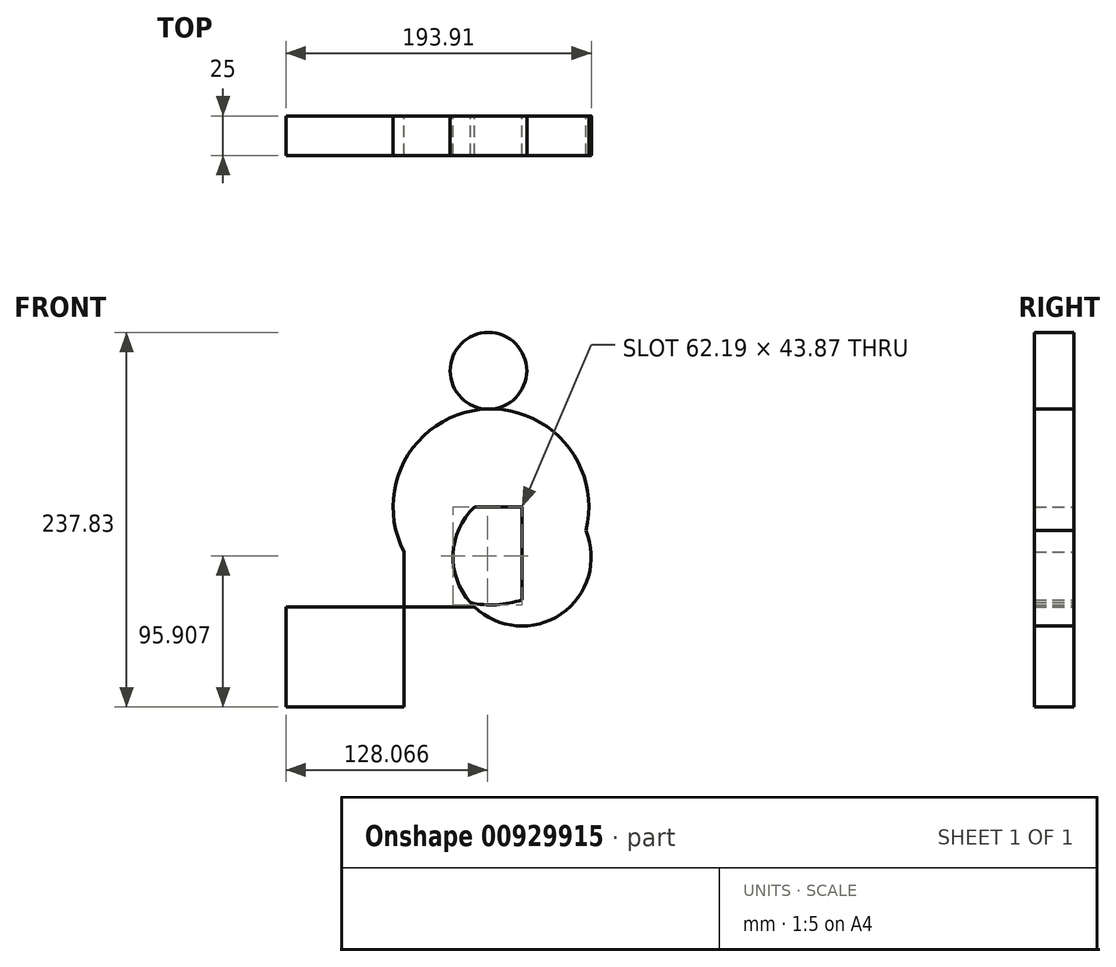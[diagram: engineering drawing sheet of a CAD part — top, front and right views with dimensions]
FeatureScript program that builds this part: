
annotation { "Feature Type Name" : "Feature", "Feature Type Description" : "" }
export const myFeature = defineFeature(function(context is Context, id is Id, definition is map)
    precondition{}
    {
        {
            var Q0;
            Q0=qCreatedBy(makeId("Front.planeOp"),FACE);
            var sketch = newSketch(context, id + "F0", { "sketchPlane" : qUnion([Q0])});
            skLineSegment(sketch, "E0.bottom", {"start": v(0, 0) * mm, "end": v(75, 0) * mm});
            skLineSegment(sketch, "E0.top", {"start": v(0, 63.5) * mm, "end": v(75, 63.5) * mm});
            skLineSegment(sketch, "E0.left", {"start": v(0, 0) * mm, "end": v(0, 63.5) * mm});
            skLineSegment(sketch, "E0.right", {"start": v(75, 0) * mm, "end": v(75, 63.5) * mm});
            skLineSegment(sketch, "E1.bottom", {"start": v(0, 0) * mm, "end": v(-75, 0) * mm});
            skLineSegment(sketch, "E1.top", {"start": v(0, -63.5) * mm, "end": v(-75, -63.5) * mm});
            skLineSegment(sketch, "E1.left", {"start": v(0, 0) * mm, "end": v(0, -63.5) * mm});
            skLineSegment(sketch, "E1.right", {"start": v(-75, 0) * mm, "end": v(-75, -63.5) * mm});
            skCircle(sketch, "E2", {"center": v(75, 31.75) * mm, "radius": 43.9 * mm});
            skCircle(sketch, "E3", {"center": v(55.22, 63.5) * mm, "radius": 62.2 * mm});
            skCircle(sketch, "E4", {"center": v(53.61, 150) * mm, "radius": 24.33 * mm});
            skSolve(sketch);
        }
        {
            var Q0;
            Q0 = qSketchRegion(id + "F0", true);
            extrude(context, id + "F1", {"entities" : qUnion([Q0]), "depth" : 25 * mm, "offsetDistance" : 25 * mm});
        }
    });
